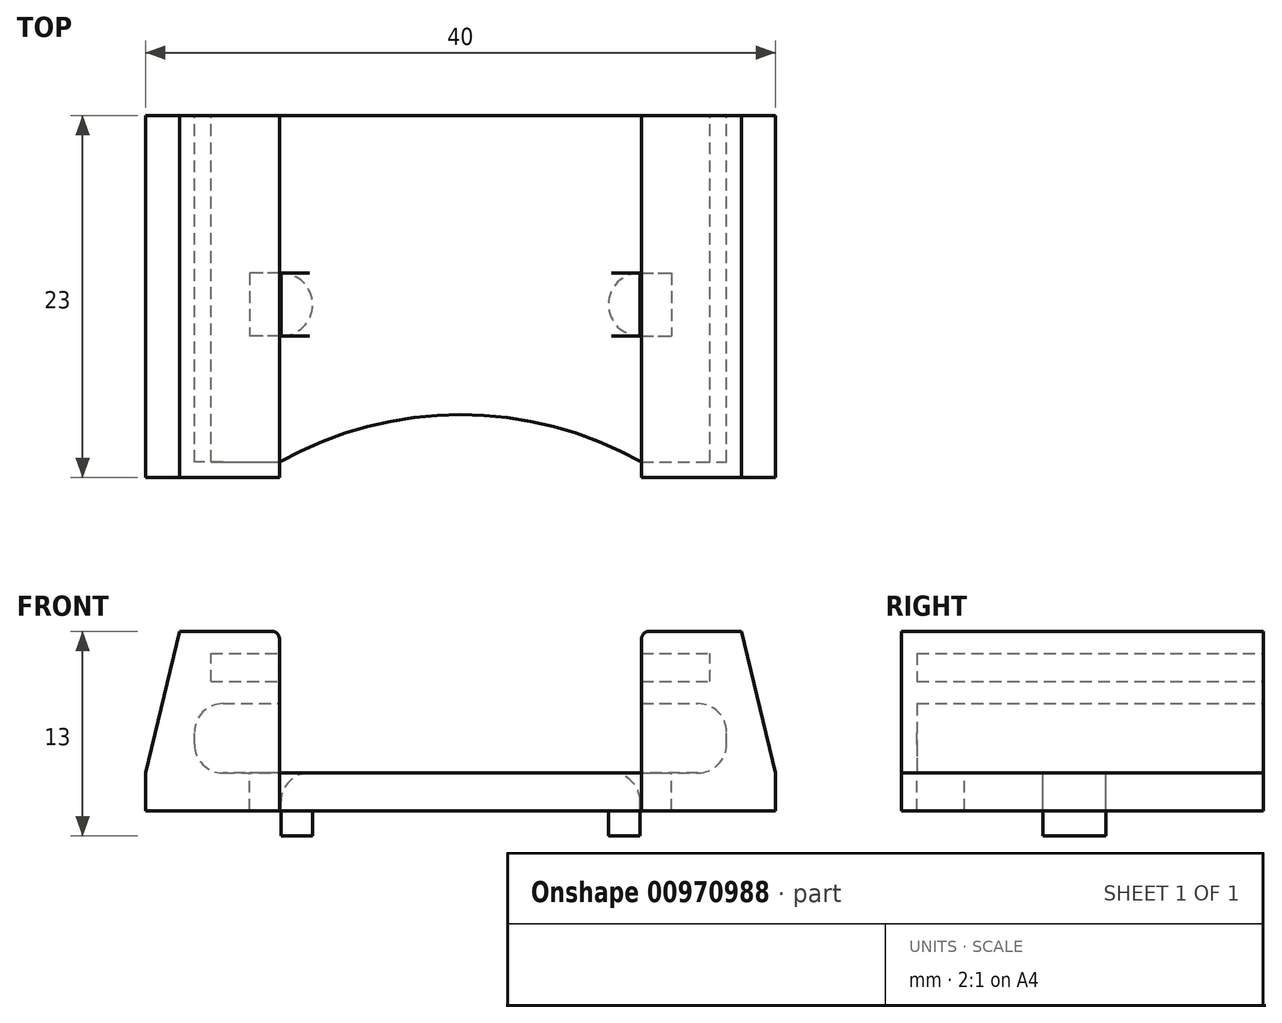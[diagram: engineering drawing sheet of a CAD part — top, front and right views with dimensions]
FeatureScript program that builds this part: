
annotation { "Feature Type Name" : "Feature", "Feature Type Description" : "" }
export const myFeature = defineFeature(function(context is Context, id is Id, definition is map)
    precondition{}
    {
        {
            var Q0;
            Q0=qCreatedBy(makeId("Top.planeOp"),FACE);
            var sketch = newSketch(context, id + "F0", { "sketchPlane" : qUnion([Q0])});
            skLineSegment(sketch, "E0.bottom", {"start": v(20, 11.5) * mm, "end": v(-20, 11.5) * mm});
            skLineSegment(sketch, "E0.top", {"start": v(20, -11.5) * mm, "end": v(-20, -11.5) * mm});
            skLineSegment(sketch, "E0.left", {"start": v(20, 11.5) * mm, "end": v(20, -11.5) * mm});
            skLineSegment(sketch, "E0.right", {"start": v(-20, 11.5) * mm, "end": v(-20, -11.5) * mm});
            skPoint(sketch, "E0.middle", {"position": v(0, 0) * mm});
            skPoint(sketch, "E1.middle", {"position": v(0, 10) * mm});
            skLineSegment(sketch, "E2.bottom", {"start": v(11.4, 1.5) * mm, "end": v(-11.4, 1.5) * mm, "construction": true});
            skLineSegment(sketch, "E2.top", {"start": v(11.4, -2.5) * mm, "end": v(-11.4, -2.5) * mm, "construction": true});
            skLineSegment(sketch, "E2.left", {"start": v(11.4, 1.5) * mm, "end": v(11.4, -2.5) * mm, "construction": true});
            skLineSegment(sketch, "E2.right", {"start": v(-11.4, 1.5) * mm, "end": v(-11.4, -2.5) * mm, "construction": true});
            skPoint(sketch, "E2.middle", {"position": v(0, -0.5) * mm});
            skArc(sketch, "E3", {"start": v(-11.4, -2.5) * mm, "mid": v(-9.4, -0.5) * mm, "end": v(-11.4, 1.5) * mm});
            skArc(sketch, "E4", {"start": v(11.4, 1.5) * mm, "mid": v(9.4, -0.5) * mm, "end": v(11.4, -2.5) * mm});
            skLineSegment(sketch, "E5", {"start": v(11.4, 1.5) * mm, "end": v(11.4, -2.5) * mm});
            skLineSegment(sketch, "E6", {"start": v(-11.4, 1.5) * mm, "end": v(-11.4, -2.5) * mm});
            skLineSegment(sketch, "E7.bottom", {"start": v(-11.4, 1.5) * mm, "end": v(-13.4, 1.5) * mm});
            skLineSegment(sketch, "E7.top", {"start": v(-11.4, -2.5) * mm, "end": v(-13.4, -2.5) * mm});
            skLineSegment(sketch, "E7.right", {"start": v(-13.4, 1.5) * mm, "end": v(-13.4, -2.5) * mm});
            skLineSegment(sketch, "E8.bottom", {"start": v(11.4, 1.5) * mm, "end": v(13.4, 1.5) * mm});
            skLineSegment(sketch, "E8.top", {"start": v(11.4, -2.5) * mm, "end": v(13.4, -2.5) * mm});
            skLineSegment(sketch, "E8.right", {"start": v(13.4, 1.5) * mm, "end": v(13.4, -2.5) * mm});
            skSolve(sketch);
        }
        {
            var Q0;
            Q0=makeQuery(id+"F0.imprint","IMPRINT",FACE,{"disambiguationData":[TD([[makeQuery(id+"F0.imprint","IMPRINT",EDGE,{"derivedFrom":sQuery(id+"F0.wireOp",EDGE,"E0.bottom")}),1.0]])]});
            var Q1;
            Q1=makeQuery(id+"F0.imprint","IMPRINT",FACE,{"disambiguationData":[TD([[makeQuery(id+"F0.imprint","IMPRINT",EDGE,{"derivedFrom":sQuery(id+"F0.wireOp",EDGE,"E3")}),1.0]])]});
            var Q2;
            Q2=makeQuery(id+"F0.imprint","IMPRINT",FACE,{"disambiguationData":[TD([[makeQuery(id+"F0.imprint","IMPRINT",EDGE,{"derivedFrom":sQuery(id+"F0.wireOp",EDGE,"E4")}),1.0]])]});
            extrude(context, id + "F1", {"entities" : qUnion([Q0, Q1, Q2]), "oppositeDirection" : true, "depth" : 2.4 * mm, "offsetDistance" : 25 * mm});
        }
        {
            var Q0;
            Q0=makeQuery(id+"F1.opExtrude","CAP_FACE",FACE,{"disambiguationData":[OSD([sQuery(id+"F0.wireOp",EDGE,"E0.bottom"),sQuery(id+"F0.wireOp",EDGE,"E0.top"),sQuery(id+"F0.wireOp",EDGE,"E0.left"),sQuery(id+"F0.wireOp",EDGE,"E0.right"),sQuery(id+"F0.wireOp",EDGE,"xqsCPxTT-J7bG-hs3p-010U-8iJFQCpX539Q.bottom"),sQuery(id+"F0.wireOp",EDGE,"xqsCPxTT-J7bG-hs3p-010U-8iJFQCpX539Q.top"),sQuery(id+"F0.wireOp",EDGE,"xqsCPxTT-J7bG-hs3p-010U-8iJFQCpX539Q.left"),sQuery(id+"F0.wireOp",EDGE,"xqsCPxTT-J7bG-hs3p-010U-8iJFQCpX539Q.right"),sQuery(id+"F0.wireOp",EDGE,"p5xQwB1T-pm26-ZWG0-hByN-pF5XrJSyHKUX.bottom"),sQuery(id+"F0.wireOp",EDGE,"p5xQwB1T-pm26-ZWG0-hByN-pF5XrJSyHKUX.top"),sQuery(id+"F0.wireOp",EDGE,"p5xQwB1T-pm26-ZWG0-hByN-pF5XrJSyHKUX.left"),sQuery(id+"F0.wireOp",EDGE,"p5xQwB1T-pm26-ZWG0-hByN-pF5XrJSyHKUX.right"),sQuery(id+"F0.wireOp",EDGE,"E7.bottom"),sQuery(id+"F0.wireOp",EDGE,"E7.top"),sQuery(id+"F0.wireOp",EDGE,"E6"),sQuery(id+"F0.wireOp",EDGE,"E7.right"),sQuery(id+"F0.wireOp",EDGE,"E8.bottom"),sQuery(id+"F0.wireOp",EDGE,"E8.top"),sQuery(id+"F0.wireOp",EDGE,"E5"),sQuery(id+"F0.wireOp",EDGE,"E8.right")])],"isStart":true});
            var sketch = newSketch(context, id + "F2", { "sketchPlane" : qUnion([Q0])});
            skLineSegment(sketch, "E9.bottom", {"start": v(20, -11.5) * mm, "end": v(11.5, -11.5) * mm});
            skLineSegment(sketch, "E9.top", {"start": v(20, 11.5) * mm, "end": v(11.5, 11.5) * mm});
            skLineSegment(sketch, "E9.left", {"start": v(20, -11.5) * mm, "end": v(20, 11.5) * mm});
            skLineSegment(sketch, "E9.right", {"start": v(11.5, -11.5) * mm, "end": v(11.5, 11.5) * mm});
            skLineSegment(sketch, "E10.bottom", {"start": v(-20, -11.5) * mm, "end": v(-11.5, -11.5) * mm});
            skLineSegment(sketch, "E10.top", {"start": v(-20, 11.5) * mm, "end": v(-11.5, 11.5) * mm});
            skLineSegment(sketch, "E10.left", {"start": v(-20, -11.5) * mm, "end": v(-20, 11.5) * mm});
            skLineSegment(sketch, "E10.right", {"start": v(-11.5, -11.5) * mm, "end": v(-11.5, 11.5) * mm});
            skSolve(sketch);
        }
        {
            var Q0;
            Q0 = qSketchRegion(id + "F2", true);
            extrude(context, id + "F3", {"entities" : qUnion([Q0]), "operationType" : NewBodyOperationType.ADD, "depth" : 9 * mm, "offsetDistance" : 25 * mm});
        }
        {
            var Q0;
            Q0=makeQuery(id+"F0.imprint","IMPRINT",FACE,{"disambiguationData":[TD([[makeQuery(id+"F0.imprint","IMPRINT",EDGE,{"derivedFrom":sQuery(id+"F0.wireOp",EDGE,"E3")}),1.0]])]});
            var Q1;
            Q1=makeQuery(id+"F0.imprint","IMPRINT",FACE,{"disambiguationData":[TD([[makeQuery(id+"F0.imprint","IMPRINT",EDGE,{"derivedFrom":sQuery(id+"F0.wireOp",EDGE,"E4")}),1.0]])]});
            extrude(context, id + "F4", {"entities" : qUnion([Q0, Q1]), "operationType" : NewBodyOperationType.ADD, "oppositeDirection" : true, "depth" : 4 * mm, "offsetDistance" : 25 * mm});
        }
        {
            var Q0;
            Q0=makeQuery(id+"F3.boolean.opBoolean","MERGE",FACE,{"derivedFrom":[makeQuery(id+"F1.opExtrude","SWEPT_FACE",FACE,{"disambiguationData":[OSD([sQuery(id+"F0.wireOp",EDGE,"E0.bottom")])]}),makeQuery(id+"F3.opExtrude","SWEPT_FACE",FACE,{"disambiguationData":[OSD([sQuery(id+"F2.wireOp",EDGE,"E9.top")])]}),makeQuery(id+"F3.opExtrude","SWEPT_FACE",FACE,{"disambiguationData":[OSD([sQuery(id+"F2.wireOp",EDGE,"E10.top")])]})]});
            var sketch = newSketch(context, id + "F5", { "sketchPlane" : qUnion([Q0])});
            skLineSegment(sketch, "E11.bottom", {"start": v(15.85, 5.8) * mm, "end": v(-15.85, 5.8) * mm});
            skLineSegment(sketch, "E11.top", {"start": v(15.85, 7.6) * mm, "end": v(-15.85, 7.6) * mm});
            skLineSegment(sketch, "E11.left", {"start": v(15.85, 5.8) * mm, "end": v(15.85, 7.6) * mm});
            skLineSegment(sketch, "E11.right", {"start": v(-15.85, 5.8) * mm, "end": v(-15.85, 7.6) * mm});
            skPoint(sketch, "E11.middle", {"position": v(0, 6.7) * mm});
            skLineSegment(sketch, "E12.bottom", {"start": v(16.9, 0) * mm, "end": v(-16.9, 0) * mm});
            skLineSegment(sketch, "E12.top", {"start": v(16.9, 4.4) * mm, "end": v(-16.9, 4.4) * mm});
            skLineSegment(sketch, "E12.left", {"start": v(16.9, 0) * mm, "end": v(16.9, 4.4) * mm});
            skLineSegment(sketch, "E12.right", {"start": v(-16.9, 0) * mm, "end": v(-16.9, 4.4) * mm});
            skPoint(sketch, "E12.middle", {"position": v(0, 2.2) * mm});
            skLineSegment(sketch, "E13", {"start": v(-20, 0) * mm, "end": v(-20, 9) * mm});
            skLineSegment(sketch, "E14", {"start": v(-20, 9) * mm, "end": v(-17.85, 9) * mm});
            skLineSegment(sketch, "E15", {"start": v(-17.85, 9) * mm, "end": v(-20, 0) * mm});
            skLineSegment(sketch, "E16.MirrorCS", {"start": v(17.85, 9) * mm, "end": v(20, 0) * mm});
            skLineSegment(sketch, "E17.MirrorCS", {"start": v(20, 0) * mm, "end": v(20, 9) * mm});
            skLineSegment(sketch, "E18.MirrorCS", {"start": v(20, 9) * mm, "end": v(17.85, 9) * mm});
            skSolve(sketch);
        }
        {
            var Q0;
            {var subQ0=sQuery(id+"F5.wireOp",EDGE,"E11.right");Q0=makeQuery(id+"F5.imprint","IMPRINT",FACE,{"disambiguationData":[TD([[makeQuery(id+"F5.imprint","IMPRINT",EDGE,{"derivedFrom":subQ0}),-1.0]])]});}
            var Q1;
            {var subQ0=sQuery(id+"F5.wireOp",EDGE,"E11.left");Q1=makeQuery(id+"F5.imprint","IMPRINT",FACE,{"disambiguationData":[TD([[makeQuery(id+"F5.imprint","IMPRINT",EDGE,{"derivedFrom":subQ0}),1.0]])]});}
            var Q2;
            {var subQ3=sQuery(id+"F5.wireOp",EDGE,"E12.left");Q2=makeQuery(id+"F5.imprint","IMPRINT",FACE,{"disambiguationData":[TD([[makeQuery(id+"F5.imprint","IMPRINT",EDGE,{"derivedFrom":subQ3}),1.0]])]});}
            var Q3;
            {var subQ3=sQuery(id+"F5.wireOp",EDGE,"E12.right");Q3=makeQuery(id+"F5.imprint","IMPRINT",FACE,{"disambiguationData":[TD([[makeQuery(id+"F5.imprint","IMPRINT",EDGE,{"derivedFrom":subQ3}),-1.0]])]});}
            extrude(context, id + "F6", {"entities" : qUnion([Q0, Q1, Q2, Q3]), "operationType" : NewBodyOperationType.REMOVE, "oppositeDirection" : true, "depth" : 22 * mm, "offsetDistance" : 25 * mm});
        }
        {
            var Q0;
            Q0=makeQuery(id+"F5.imprint","IMPRINT",FACE,{"disambiguationData":[TD([[makeQuery(id+"F5.imprint","IMPRINT",EDGE,{"derivedFrom":sQuery(id+"F5.wireOp",EDGE,"E13")}),-1.0]])]});
            var Q1;
            Q1=makeQuery(id+"F5.imprint","IMPRINT",FACE,{"disambiguationData":[TD([[makeQuery(id+"F5.imprint","IMPRINT",EDGE,{"derivedFrom":sQuery(id+"F5.wireOp",EDGE,"E16.MirrorCS")}),1.0]])]});
            extrude(context, id + "F7", {"entities" : qUnion([Q0, Q1]), "operationType" : NewBodyOperationType.REMOVE, "endBound" : BoundingType.THROUGH_ALL, "oppositeDirection" : true, "depth" : 25 * mm, "offsetDistance" : 25 * mm});
        }
        {
            var Q0;
            Q0=makeQuery(id+"F7.boolean.opBoolean","COPY",EDGE,{"derivedFrom":makeQuery(id+"F7.opExtrude","SWEPT_EDGE",EDGE,{"disambiguationData":[OSD([sQuery(id+"F0.wireOp",EDGE,"E0.bottom"),sQuery(id+"F0.wireOp",EDGE,"E0.left"),sQuery(id+"F2.wireOp",EDGE,"E9.top"),sQuery(id+"F2.wireOp",EDGE,"E9.left"),sQuery(id+"F5.wireOp",EDGE,"E13"),sQuery(id+"F5.wireOp",EDGE,"E15")])]})});
            var Q1;
            Q1=makeQuery(id+"F7.boolean.opBoolean","COPY",EDGE,{"derivedFrom":makeQuery(id+"F7.opExtrude","SWEPT_EDGE",EDGE,{"disambiguationData":[OSD([sQuery(id+"F2.wireOp",EDGE,"E9.top"),sQuery(id+"F5.wireOp",EDGE,"E14"),sQuery(id+"F5.wireOp",EDGE,"E15")])]})});
            var Q2;
            Q2=makeQuery(id+"F7.boolean.opBoolean","COPY",EDGE,{"derivedFrom":makeQuery(id+"F7.opExtrude","SWEPT_EDGE",EDGE,{"disambiguationData":[OSD([sQuery(id+"F2.wireOp",EDGE,"E10.top"),sQuery(id+"F5.wireOp",EDGE,"E16.MirrorCS"),sQuery(id+"F5.wireOp",EDGE,"E18.MirrorCS")])]})});
            var Q3;
            Q3=makeQuery(id+"F7.boolean.opBoolean","COPY",EDGE,{"derivedFrom":makeQuery(id+"F7.opExtrude","SWEPT_EDGE",EDGE,{"disambiguationData":[OSD([sQuery(id+"F0.wireOp",EDGE,"E0.bottom"),sQuery(id+"F0.wireOp",EDGE,"E0.right"),sQuery(id+"F2.wireOp",EDGE,"E10.top"),sQuery(id+"F2.wireOp",EDGE,"E10.left"),sQuery(id+"F5.wireOp",EDGE,"E16.MirrorCS"),sQuery(id+"F5.wireOp",EDGE,"E17.MirrorCS")])]})});
            var Q4;
            {var subQ0=sQuery(id+"F5.wireOp",EDGE,"E12.bottom");var subQ3=sQuery(id+"F0.wireOp",EDGE,"p5xQwB1T-pm26-ZWG0-hByN-pF5XrJSyHKUX.top");var subQ4=sQuery(id+"F5.wireOp",EDGE,"E12.right");Q4=makeQuery(id+"F6.boolean.opBoolean","COPY",EDGE,{"disambiguationData":[TD([makeQuery(id+"F1.opExtrude","SWEPT_FACE",FACE,{"disambiguationData":[OSD([subQ3])]})])],"derivedFrom":makeQuery(id+"F6.opExtrude","SWEPT_EDGE",EDGE,{"disambiguationData":[OSD([subQ0,subQ4])]})});}
            var Q5;
            Q5=makeQuery(id+"F6.boolean.opBoolean","COPY",EDGE,{"derivedFrom":makeQuery(id+"F6.opExtrude","SWEPT_EDGE",EDGE,{"disambiguationData":[OSD([sQuery(id+"F5.wireOp",EDGE,"E12.top"),sQuery(id+"F5.wireOp",EDGE,"E12.right")])]})});
            var Q6;
            Q6=makeQuery(id+"F6.boolean.opBoolean","COPY",EDGE,{"derivedFrom":makeQuery(id+"F6.opExtrude","SWEPT_EDGE",EDGE,{"disambiguationData":[OSD([sQuery(id+"F5.wireOp",EDGE,"E12.top"),sQuery(id+"F5.wireOp",EDGE,"E12.left")])]})});
            var Q7;
            {var subQ0=sQuery(id+"F5.wireOp",EDGE,"E12.bottom");var subQ4=sQuery(id+"F5.wireOp",EDGE,"E12.left");var subQ6=sQuery(id+"F0.wireOp",EDGE,"xqsCPxTT-J7bG-hs3p-010U-8iJFQCpX539Q.top");Q7=makeQuery(id+"F6.boolean.opBoolean","COPY",EDGE,{"disambiguationData":[TD([makeQuery(id+"F1.opExtrude","SWEPT_FACE",FACE,{"disambiguationData":[OSD([subQ6])]})])],"derivedFrom":makeQuery(id+"F6.opExtrude","SWEPT_EDGE",EDGE,{"disambiguationData":[OSD([subQ0,subQ4])]})});}
            var Q8;
            Q8=makeQuery(id+"F1.opExtrude","CAP_EDGE",EDGE,{"disambiguationData":[OSD([sQuery(id+"F0.wireOp",EDGE,"E6")])],"isStart":true});
            var Q9;
            Q9=makeQuery(id+"F1.opExtrude","CAP_EDGE",EDGE,{"disambiguationData":[OSD([sQuery(id+"F0.wireOp",EDGE,"E5")])],"isStart":true});
            var Q10;
            Q10=makeQuery(id+"F6.boolean.opBoolean","COPY",EDGE,{"derivedFrom":makeQuery(id+"F6.opExtrude","SWEPT_EDGE",EDGE,{"disambiguationData":[OSD([sQuery(id+"F0.wireOp",EDGE,"E0.bottom"),sQuery(id+"F2.wireOp",EDGE,"E10.top"),sQuery(id+"F2.wireOp",EDGE,"E10.right"),sQuery(id+"F5.wireOp",EDGE,"E12.top")])]})});
            var Q11;
            Q11=makeQuery(id+"F6.boolean.opBoolean","COPY",EDGE,{"derivedFrom":makeQuery(id+"F6.opExtrude","SWEPT_EDGE",EDGE,{"disambiguationData":[OSD([sQuery(id+"F0.wireOp",EDGE,"E0.bottom"),sQuery(id+"F2.wireOp",EDGE,"E9.top"),sQuery(id+"F2.wireOp",EDGE,"E9.right"),sQuery(id+"F5.wireOp",EDGE,"E12.top")])]})});
            fillet(context, id + "F8", {"entities" : qUnion([Q0, Q1, Q2, Q3, Q4, Q5, Q6, Q7, Q8, Q9, Q10, Q11]), "radius" : 1.8 * mm, "tangentPropagation" : true, "allowEdgeOverflow" : false});
        }
        {
            var Q0;
            Q0=makeQuery(id+"F6.boolean.opBoolean","COPY",EDGE,{"derivedFrom":makeQuery(id+"F6.opExtrude","CAP_EDGE",EDGE,{"disambiguationData":[OSD([sQuery(id+"F5.wireOp",EDGE,"E11.left")])],"isStart":true})});
            var Q1;
            {var subQ0=sQuery(id+"F5.wireOp",EDGE,"E11.top");Q1=makeQuery(id+"F6.boolean.opBoolean","COPY",EDGE,{"derivedFrom":makeQuery(id+"F6.opExtrude","CAP_EDGE",EDGE,{"disambiguationData":[OSD([subQ0]),TDD([makeQuery(id+"F5.imprint","IMPRINT",EDGE,{"disambiguationData":[TD([[makeQuery(id+"F5.imprint","INTERSECT",VERTEX,{"derivedFrom":[subQ0,sQuery(id+"F5.wireOp",EDGE,"E11.left")]}),-1.0]])],"derivedFrom":subQ0})])],"isStart":true})});}
            var Q2;
            {var subQ0=sQuery(id+"F5.wireOp",EDGE,"E11.bottom");Q2=makeQuery(id+"F6.boolean.opBoolean","COPY",EDGE,{"derivedFrom":makeQuery(id+"F6.opExtrude","CAP_EDGE",EDGE,{"disambiguationData":[OSD([subQ0]),TDD([makeQuery(id+"F5.imprint","IMPRINT",EDGE,{"disambiguationData":[TD([[makeQuery(id+"F5.imprint","INTERSECT",VERTEX,{"derivedFrom":[subQ0,sQuery(id+"F5.wireOp",EDGE,"E11.left")]}),-1.0]])],"derivedFrom":subQ0})])],"isStart":true})});}
            var Q3;
            {var subQ0=sQuery(id+"F5.wireOp",EDGE,"E11.bottom");Q3=makeQuery(id+"F6.boolean.opBoolean","COPY",EDGE,{"derivedFrom":makeQuery(id+"F6.opExtrude","CAP_EDGE",EDGE,{"disambiguationData":[OSD([subQ0]),TDD([makeQuery(id+"F5.imprint","IMPRINT",EDGE,{"disambiguationData":[TD([[makeQuery(id+"F5.imprint","INTERSECT",VERTEX,{"derivedFrom":[subQ0,sQuery(id+"F5.wireOp",EDGE,"E11.right")]}),1.0]])],"derivedFrom":subQ0})])],"isStart":true})});}
            var Q4;
            {var subQ0=sQuery(id+"F5.wireOp",EDGE,"E11.top");Q4=makeQuery(id+"F6.boolean.opBoolean","COPY",EDGE,{"derivedFrom":makeQuery(id+"F6.opExtrude","CAP_EDGE",EDGE,{"disambiguationData":[OSD([subQ0]),TDD([makeQuery(id+"F5.imprint","IMPRINT",EDGE,{"disambiguationData":[TD([[makeQuery(id+"F5.imprint","INTERSECT",VERTEX,{"derivedFrom":[subQ0,sQuery(id+"F5.wireOp",EDGE,"E11.right")]}),1.0]])],"derivedFrom":subQ0})])],"isStart":true})});}
            var Q5;
            Q5=makeQuery(id+"F6.boolean.opBoolean","COPY",EDGE,{"derivedFrom":makeQuery(id+"F6.opExtrude","CAP_EDGE",EDGE,{"disambiguationData":[OSD([sQuery(id+"F5.wireOp",EDGE,"E11.right")])],"isStart":true})});
            var Q6;
            Q6=makeQuery(id+"F3.opExtrude","CAP_EDGE",EDGE,{"disambiguationData":[OSD([sQuery(id+"F2.wireOp",EDGE,"E9.right")])],"isStart":false});
            var Q7;
            Q7=makeQuery(id+"F3.opExtrude","CAP_EDGE",EDGE,{"disambiguationData":[OSD([sQuery(id+"F2.wireOp",EDGE,"E10.right")])],"isStart":false});
            var Q8;
            {var subQ0=sQuery(id+"F5.wireOp",EDGE,"E12.bottom");var subQ1=sQuery(id+"F0.wireOp",EDGE,"E0.bottom");Q8=makeQuery(id+"F6.boolean.opBoolean","MERGE",EDGE,{"derivedFrom":[makeQuery(id+"F1.opExtrude","CAP_EDGE",EDGE,{"disambiguationData":[OSD([subQ1])],"isStart":true})],"fromTools":[makeQuery(id+"F6.opExtrude","CAP_EDGE",EDGE,{"disambiguationData":[OSD([subQ0]),TDD([makeQuery(id+"F5.imprint","IMPRINT",EDGE,{"disambiguationData":[TD([[makeQuery(id+"F5.imprint","INTERSECT",VERTEX,{"derivedFrom":[makeQuery(id+"F3.opExtrude","SWEPT_EDGE",EDGE,{"disambiguationData":[OSD([subQ1,sQuery(id+"F2.wireOp",EDGE,"E10.top"),sQuery(id+"F2.wireOp",EDGE,"E10.right")])]}),subQ0]}),1.0],[makeQuery(id+"F5.imprint","INTERSECT",VERTEX,{"derivedFrom":[subQ0,sQuery(id+"F5.wireOp",EDGE,"E12.left")]}),-1.0]])],"derivedFrom":subQ0})])],"isStart":true}),makeQuery(id+"F6.opExtrude","CAP_EDGE",EDGE,{"disambiguationData":[OSD([subQ0]),TDD([makeQuery(id+"F5.imprint","IMPRINT",EDGE,{"disambiguationData":[TD([[makeQuery(id+"F5.imprint","INTERSECT",VERTEX,{"derivedFrom":[makeQuery(id+"F3.opExtrude","SWEPT_EDGE",EDGE,{"disambiguationData":[OSD([subQ1,sQuery(id+"F2.wireOp",EDGE,"E9.top"),sQuery(id+"F2.wireOp",EDGE,"E9.right")])]}),subQ0]}),-1.0],[makeQuery(id+"F5.imprint","INTERSECT",VERTEX,{"derivedFrom":[subQ0,sQuery(id+"F5.wireOp",EDGE,"E12.right")]}),1.0]])],"derivedFrom":subQ0})])],"isStart":true})]});}
            fillet(context, id + "F9", {"entities" : qUnion([Q0, Q1, Q2, Q3, Q4, Q5, Q6, Q7, Q8]), "radius" : 0.5 * mm, "tangentPropagation" : true, "allowEdgeOverflow" : false});
        }
        {
            var Q0;
            Q0=makeQuery(id+"F0.imprint","IMPRINT",FACE,{"disambiguationData":[TD([[makeQuery(id+"F0.imprint","IMPRINT",EDGE,{"derivedFrom":sQuery(id+"F0.wireOp",EDGE,"E0.bottom")}),1.0]])]});
            var sketch = newSketch(context, id + "F10", { "sketchPlane" : qUnion([Q0])});
            skPoint(sketch, "E19.0", {"position": v(-11.5, -10.5) * mm});
            skPoint(sketch, "E20.0", {"position": v(11.5, -10.5) * mm});
            skArc(sketch, "E21", {"start": v(11.5, -10.5) * mm, "mid": v(0, -7.5) * mm, "end": v(-11.5, -10.5) * mm});
            skLineSegment(sketch, "E22", {"start": v(-11.5, -10.5) * mm, "end": v(-11.5, -11.5) * mm});
            skLineSegment(sketch, "E23", {"start": v(-11.5, -11.5) * mm, "end": v(11.5, -11.5) * mm});
            skLineSegment(sketch, "E24", {"start": v(11.5, -11.5) * mm, "end": v(11.5, -10.5) * mm});
            skSolve(sketch);
        }
        {
            var Q0;
            Q0 = qSketchRegion(id + "F10", true);
            extrude(context, id + "F11", {"entities" : qUnion([Q0]), "operationType" : NewBodyOperationType.REMOVE, "endBound" : BoundingType.THROUGH_ALL, "oppositeDirection" : true, "depth" : 25 * mm, "offsetDistance" : 25 * mm});
        }
    });
